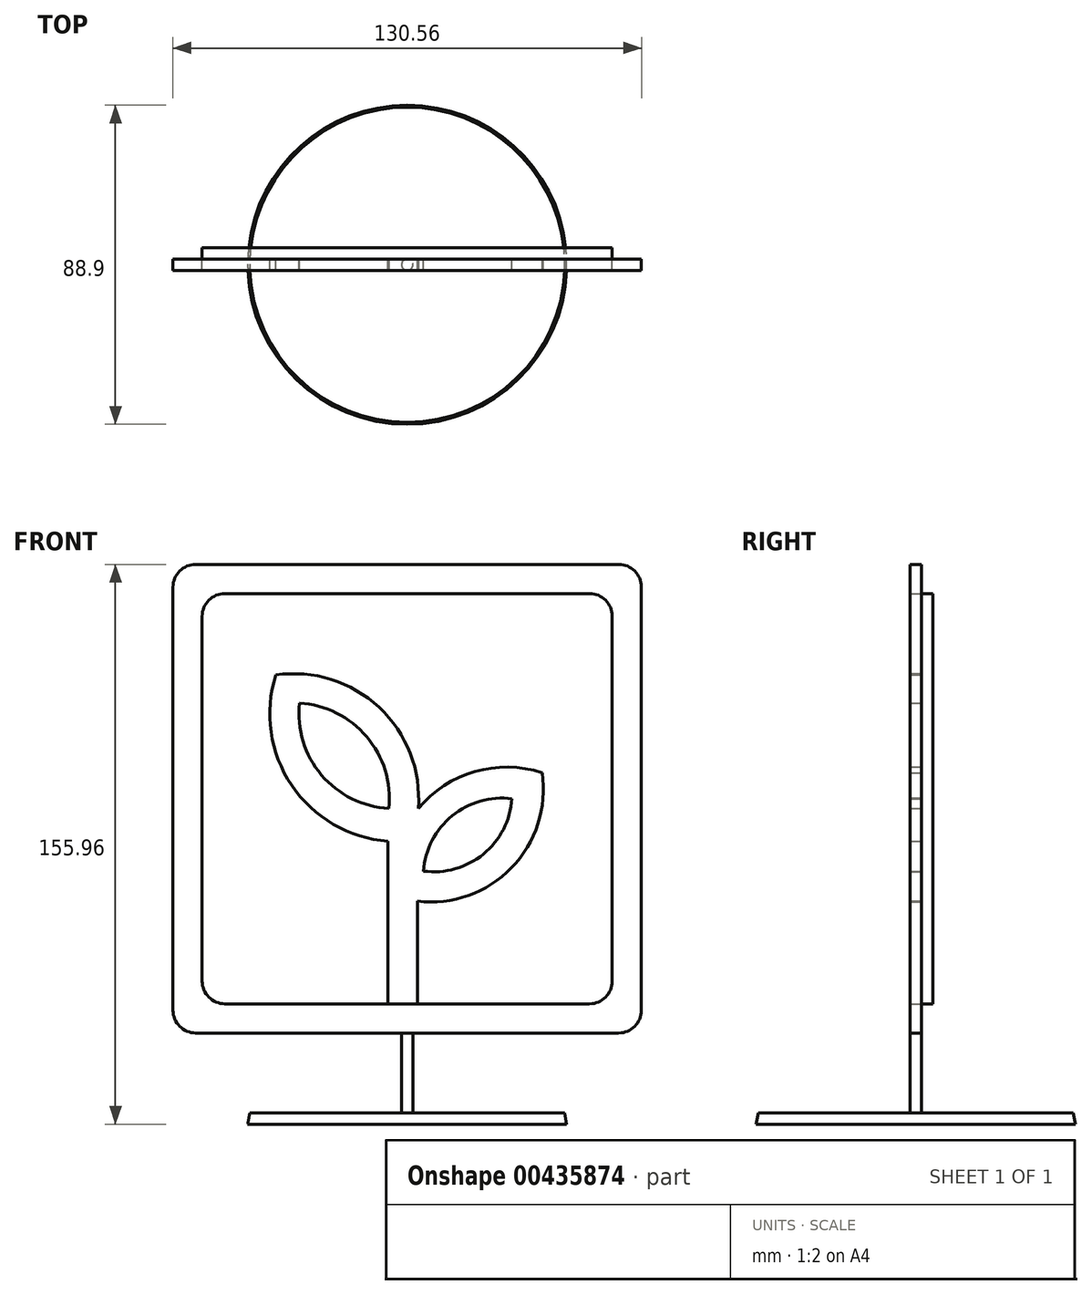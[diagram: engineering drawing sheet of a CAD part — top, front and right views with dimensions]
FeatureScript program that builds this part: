
annotation { "Feature Type Name" : "Feature", "Feature Type Description" : "" }
export const myFeature = defineFeature(function(context is Context, id is Id, definition is map)
    precondition{}
    {
        {
            var Q0;
            Q0=qCreatedBy(makeId("Front.planeOp"),FACE);
            var sketch = newSketch(context, id + "F0", { "sketchPlane" : qUnion([Q0])});
            skLineSegment(sketch, "E0", {"start": v(0, 67.9) * mm, "end": v(0, -67.43) * mm, "construction": true});
            skLineSegment(sketch, "E1", {"start": v(-68.62, 0) * mm, "end": v(68.14, 0) * mm, "construction": true});
            skLineSegment(sketch, "E2.bottom", {"start": v(-50.8, 57.15) * mm, "end": v(50.8, 57.15) * mm});
            skLineSegment(sketch, "E2.top", {"start": v(-50.8, -57.15) * mm, "end": v(50.8, -57.15) * mm});
            skLineSegment(sketch, "E2.left", {"start": v(-57.15, 50.8) * mm, "end": v(-57.15, -50.8) * mm});
            skLineSegment(sketch, "E2.right", {"start": v(57.15, 50.8) * mm, "end": v(57.15, -50.8) * mm});
            skPoint(sketch, "E3.visualSharp", {"position": v(-57.15, 57.15) * mm});
            skArc(sketch, "E3.filletArc", {"start": v(-50.8, 57.15) * mm, "mid": v(-55.3, 55.3) * mm, "end": v(-57.15, 50.8) * mm});
            skPoint(sketch, "E4.visualSharp", {"position": v(-57.15, -57.15) * mm});
            skArc(sketch, "E4.filletArc", {"start": v(-57.15, -50.8) * mm, "mid": v(-55.3, -55.3) * mm, "end": v(-50.8, -57.15) * mm});
            skPoint(sketch, "E5.visualSharp", {"position": v(57.15, -57.15) * mm});
            skArc(sketch, "E5.filletArc", {"start": v(50.8, -57.15) * mm, "mid": v(55.3, -55.3) * mm, "end": v(57.15, -50.8) * mm});
            skPoint(sketch, "E6.visualSharp", {"position": v(57.15, 57.15) * mm});
            skArc(sketch, "E6.filletArc", {"start": v(57.15, 50.8) * mm, "mid": v(55.3, 55.3) * mm, "end": v(50.8, 57.15) * mm});
            skSolve(sketch);
        }
        {
            var Q0;
            Q0=qCreatedBy(makeId("Front.planeOp"),FACE);
            var sketch = newSketch(context, id + "F1", { "sketchPlane" : qUnion([Q0])});
            skLineSegment(sketch, "E7", {"start": v(-5.39, -57.15) * mm, "end": v(-5.39, -11.84) * mm});
            skArc(sketch, "E8", {"start": v(4.55, -20.2) * mm, "mid": v(21.24, -15.43) * mm, "end": v(29.17, 0) * mm});
            skArc(sketch, "E9", {"start": v(29.17, 0) * mm, "mid": v(12.5, -4.79) * mm, "end": v(4.55, -20.2) * mm});
            skPoint(sketch, "E10", {"position": v(37.6, 7.23) * mm});
            skPoint(sketch, "E11", {"position": v(3.09, -2.73) * mm});
            skPoint(sketch, "E12", {"position": v(-5.1, -2.73) * mm});
            skPoint(sketch, "E13", {"position": v(-36.64, 34.45) * mm});
            skPoint(sketch, "E14", {"position": v(-30.02, 26.63) * mm});
            skArc(sketch, "E15", {"start": v(2.84, -28.56) * mm, "mid": v(29.07, -19.26) * mm, "end": v(37.6, 7.23) * mm});
            skArc(sketch, "E16", {"start": v(37.6, 7.23) * mm, "mid": v(18.83, 7.52) * mm, "end": v(3.09, -2.73) * mm});
            skArc(sketch, "E17", {"start": v(-5.1, -2.73) * mm, "mid": v(-11.3, 17.27) * mm, "end": v(-30.02, 26.63) * mm});
            skArc(sketch, "E18", {"start": v(-30.02, 26.63) * mm, "mid": v(-23.9, 6.59) * mm, "end": v(-5.1, -2.73) * mm});
            skArc(sketch, "E19", {"start": v(-36.64, 34.45) * mm, "mid": v(-32.21, 3.74) * mm, "end": v(-5.39, -11.84) * mm});
            skArc(sketch, "E20", {"start": v(3.09, -2.73) * mm, "mid": v(-7.83, 25.42) * mm, "end": v(-36.64, 34.45) * mm});
            skLineSegment(sketch, "E21.bottom", {"start": v(-50.8, 57.15) * mm, "end": v(50.8, 57.15) * mm});
            skLineSegment(sketch, "E21.top", {"start": v(-50.8, -57.15) * mm, "end": v(-5.39, -57.15) * mm});
            skLineSegment(sketch, "E21.left", {"start": v(-57.15, 50.8) * mm, "end": v(-57.15, -50.8) * mm});
            skLineSegment(sketch, "E21.right", {"start": v(57.15, 50.8) * mm, "end": v(57.15, -50.8) * mm});
            skArc(sketch, "E22.filletArc", {"start": v(-57.15, -50.8) * mm, "mid": v(-55.3, -55.3) * mm, "end": v(-50.8, -57.15) * mm});
            skPoint(sketch, "E23.visualSharp", {"position": v(-57.15, 57.15) * mm});
            skArc(sketch, "E23.filletArc", {"start": v(-50.8, 57.15) * mm, "mid": v(-55.3, 55.3) * mm, "end": v(-57.15, 50.8) * mm});
            skPoint(sketch, "E24.visualSharp", {"position": v(57.15, 57.15) * mm});
            skArc(sketch, "E24.filletArc", {"start": v(57.15, 50.8) * mm, "mid": v(55.3, 55.3) * mm, "end": v(50.8, 57.15) * mm});
            skArc(sketch, "E25.filletArc", {"start": v(50.8, -57.15) * mm, "mid": v(55.3, -55.3) * mm, "end": v(57.15, -50.8) * mm});
            skLineSegment(sketch, "E26", {"start": v(2.84, -28.56) * mm, "end": v(2.84, -57.15) * mm});
            skLineSegment(sketch, "E27.bottom", {"start": v(-58.93, 65.28) * mm, "end": v(58.93, 65.28) * mm});
            skLineSegment(sketch, "E27.top", {"start": v(-58.93, -65.28) * mm, "end": v(58.93, -65.28) * mm});
            skLineSegment(sketch, "E27.left", {"start": v(-65.28, 58.93) * mm, "end": v(-65.28, -58.93) * mm});
            skLineSegment(sketch, "E27.right", {"start": v(65.28, 58.93) * mm, "end": v(65.28, -58.93) * mm});
            skPoint(sketch, "E28.visualSharp", {"position": v(-65.28, 65.28) * mm});
            skArc(sketch, "E28.filletArc", {"start": v(-58.93, 65.28) * mm, "mid": v(-63.42, 63.42) * mm, "end": v(-65.28, 58.93) * mm});
            skPoint(sketch, "E29.visualSharp", {"position": v(-65.28, -65.28) * mm});
            skArc(sketch, "E29.filletArc", {"start": v(-65.28, -58.93) * mm, "mid": v(-63.42, -63.42) * mm, "end": v(-58.93, -65.28) * mm});
            skPoint(sketch, "E30.visualSharp", {"position": v(65.28, -65.28) * mm});
            skArc(sketch, "E30.filletArc", {"start": v(58.93, -65.28) * mm, "mid": v(63.42, -63.42) * mm, "end": v(65.28, -58.93) * mm});
            skPoint(sketch, "E31.visualSharp", {"position": v(65.28, 65.28) * mm});
            skArc(sketch, "E31.filletArc", {"start": v(65.28, 58.93) * mm, "mid": v(63.42, 63.42) * mm, "end": v(58.93, 65.28) * mm});
            skLineSegment(sketch, "E32.trimOffspring", {"start": v(2.84, -57.15) * mm, "end": v(50.8, -57.15) * mm});
            skSolve(sketch);
        }
        {
            var Q0;
            Q0 = qSketchRegion(id + "F1", true);
            extrude(context, id + "F2", {"entities" : qUnion([Q0]), "depth" : 3.17 * mm});
        }
        {
            var Q0;
            Q0=makeQuery(id+"F2.opExtrude","SWEPT_FACE",FACE,{"disambiguationData":[OSD([sQuery(id+"F1.wireOp",EDGE,"E27.top")])]});
            var sketch = newSketch(context, id + "F3", { "sketchPlane" : qUnion([Q0])});
            skCircle(sketch, "E33", {"center": v(0, 1.59) * mm, "radius": 1.59 * mm});
            skSolve(sketch);
        }
        {
            var Q0;
            Q0 = qSketchRegion(id + "F3", true);
            extrude(context, id + "F4", {"entities" : qUnion([Q0]), "operationType" : NewBodyOperationType.ADD, "depth" : 25.4 * mm});
        }
        {
            var Q0;
            Q0=makeQuery(id+"F4.opExtrude","CAP_FACE",FACE,{"disambiguationData":[OSD([sQuery(id+"F3.wireOp",EDGE,"E33")])],"isStart":false});
            var sketch = newSketch(context, id + "F5", { "sketchPlane" : qUnion([Q0])});
            skCircle(sketch, "E34", {"center": v(0, 1.59) * mm, "radius": 44.45 * mm});
            skSolve(sketch);
        }
        {
            var Q0;
            Q0 = qSketchRegion(id + "F5", true);
            extrude(context, id + "F6", {"entities" : qUnion([Q0]), "operationType" : NewBodyOperationType.ADD, "oppositeDirection" : true, "depth" : 3.17 * mm, "hasDraft" : true, "draftAngle" : 10 * degree, "draftPullDirection" : true});
        }
        {
            var Q0;
            Q0 = qSketchRegion(id + "F0", true);
            extrude(context, id + "F7", {"entities" : qUnion([Q0]), "endBound" : BoundingType.SYMMETRIC, "depth" : 6.35 * mm});
        }
    });
